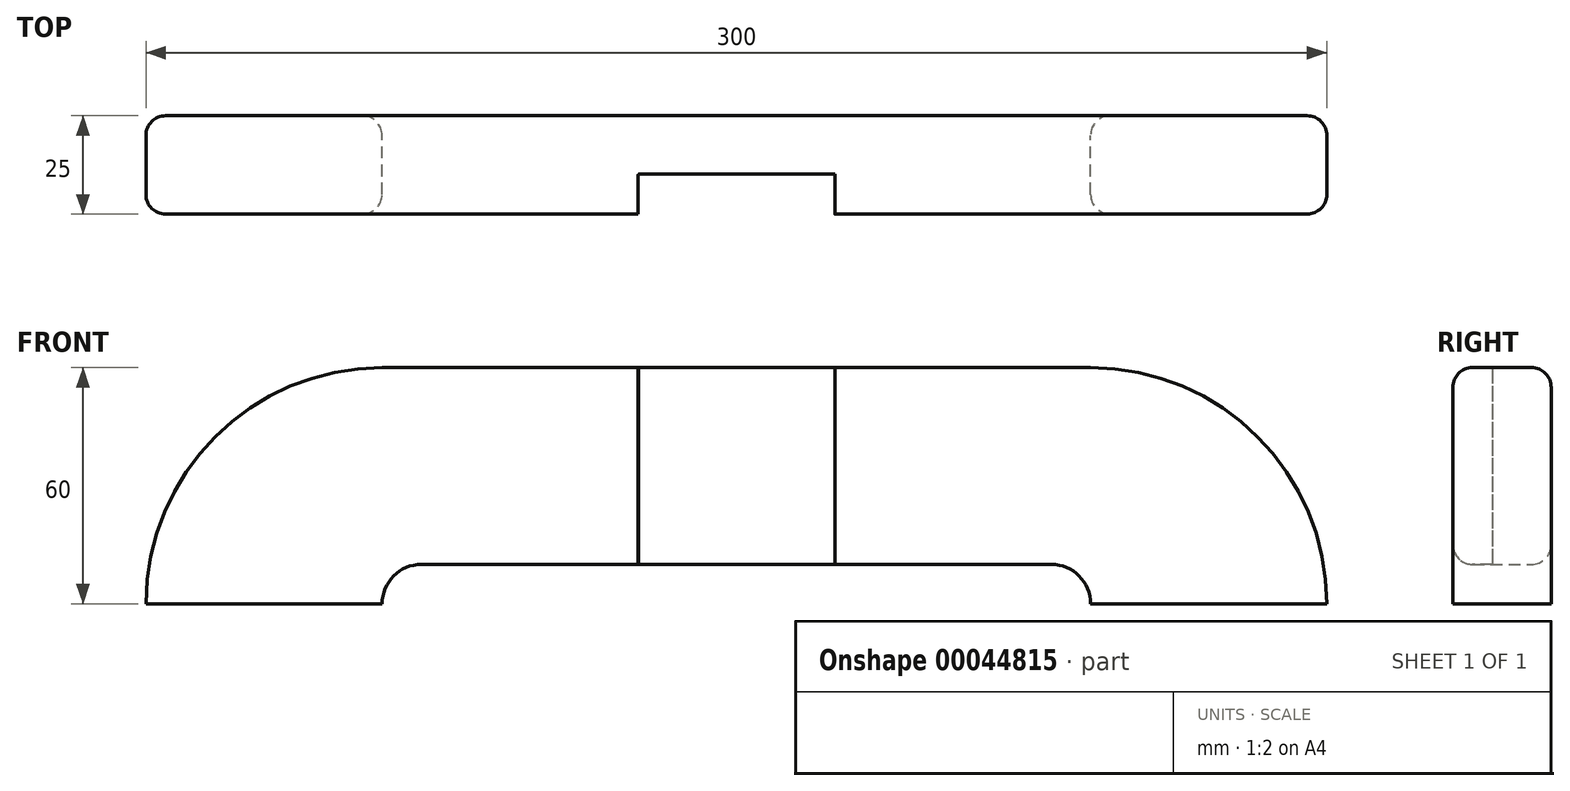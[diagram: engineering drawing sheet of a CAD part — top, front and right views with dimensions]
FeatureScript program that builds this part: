
annotation { "Feature Type Name" : "Feature", "Feature Type Description" : "" }
export const myFeature = defineFeature(function(context is Context, id is Id, definition is map)
    precondition{}
    {
        {
            var Q0;
            Q0=qCreatedBy(makeId("Front.planeOp"),FACE);
            var sketch = newSketch(context, id + "F0", { "sketchPlane" : qUnion([Q0])});
            skLineSegment(sketch, "E0.rect.bottom", {"start": v(90, 25) * mm, "end": v(-90, 25) * mm});
            skLineSegment(sketch, "E0.rect.top", {"start": v(90, -25) * mm, "end": v(-90, -25) * mm});
            skLineSegment(sketch, "E0.rect.left", {"start": v(90, 25) * mm, "end": v(90, -25) * mm});
            skLineSegment(sketch, "E0.rect.right", {"start": v(-90, 25) * mm, "end": v(-90, -25) * mm});
            skPoint(sketch, "E0.rect.middle", {"position": v(0, 0) * mm});
            skLineSegment(sketch, "E1.bottom", {"start": v(-90, 25) * mm, "end": v(-150, 25) * mm});
            skLineSegment(sketch, "E1.top", {"start": v(-90, -35) * mm, "end": v(-150, -35) * mm});
            skLineSegment(sketch, "E1.left", {"start": v(-90, 25) * mm, "end": v(-90, -35) * mm});
            skLineSegment(sketch, "E1.right", {"start": v(-150, 25) * mm, "end": v(-150, -35) * mm});
            skLineSegment(sketch, "E2", {"start": v(0, 42) * mm, "end": v(0, -72.64) * mm});
            skPoint(sketch, "E2.endSnap0", {"position": v(0, -25) * mm});
            skLineSegment(sketch, "E3.MirrorCS", {"start": v(90, 25) * mm, "end": v(90, -35) * mm});
            skLineSegment(sketch, "E4.MirrorCS", {"start": v(90, 25) * mm, "end": v(150, 25) * mm});
            skLineSegment(sketch, "E5.MirrorCS", {"start": v(90, -35) * mm, "end": v(150, -35) * mm});
            skLineSegment(sketch, "E6.MirrorCS", {"start": v(150, 25) * mm, "end": v(150, -35) * mm});
            skSolve(sketch);
        }
        {
            var Q0;
            Q0 = qSketchRegion(id + "F0", true);
            extrude(context, id + "F1", {"entities" : qUnion([Q0]), "depth" : 25 * mm});
        }
        {
            var Q0;
            Q0=makeQuery(id+"F1.opExtrude","SWEPT_EDGE",EDGE,{"disambiguationData":[OSD([sQuery(id+"F0.wireOp",EDGE,"E1.bottom"),sQuery(id+"F0.wireOp",EDGE,"E1.right")])]});
            fillet(context, id + "F2", {"entities" : qUnion([Q0]), "radius" : 60 * mm, "tangentPropagation" : true, "allowEdgeOverflow" : false});
        }
        {
            var Q0;
            Q0=makeQuery(id+"F1.opExtrude","SWEPT_EDGE",EDGE,{"disambiguationData":[OSD([sQuery(id+"F0.wireOp",EDGE,"E0.rect.top"),sQuery(id+"F0.wireOp",EDGE,"E1.left")])]});
            fillet(context, id + "F3", {"entities" : qUnion([Q0]), "radius" : 10 * mm, "tangentPropagation" : true, "allowEdgeOverflow" : false});
        }
        {
            var Q0;
            Q0=makeQuery(id+"F1.opExtrude","SWEPT_EDGE",EDGE,{"disambiguationData":[OSD([sQuery(id+"F0.wireOp",EDGE,"E0.rect.top"),sQuery(id+"F0.wireOp",EDGE,"E3.MirrorCS")])]});
            fillet(context, id + "F4", {"entities" : qUnion([Q0]), "radius" : 10 * mm, "tangentPropagation" : true, "allowEdgeOverflow" : false});
        }
        {
            var Q0;
            Q0=makeQuery(id+"F1.opExtrude","SWEPT_EDGE",EDGE,{"disambiguationData":[OSD([sQuery(id+"F0.wireOp",EDGE,"E4.MirrorCS"),sQuery(id+"F0.wireOp",EDGE,"E6.MirrorCS")])]});
            fillet(context, id + "F5", {"entities" : qUnion([Q0]), "radius" : 60 * mm, "tangentPropagation" : true, "allowEdgeOverflow" : false});
        }
        {
            var Q0;
            {var subQ0=sQuery(id+"F0.wireOp",EDGE,"E4.MirrorCS");var subQ1=sQuery(id+"F0.wireOp",EDGE,"E6.MirrorCS");Q0=makeQuery(id+"F5.opFillet","BLEND_EDGE",EDGE,{"blendedFrom":[makeQuery(id+"F1.opExtrude","SWEPT_EDGE",EDGE,{"disambiguationData":[OSD([subQ0,subQ1])]}),makeQuery(id+"F1.opExtrude","CAP_FACE",FACE,{"disambiguationData":[OSD([sQuery(id+"F0.wireOp",EDGE,"E0.rect.bottom"),sQuery(id+"F0.wireOp",EDGE,"E0.rect.top"),sQuery(id+"F0.wireOp",EDGE,"E1.bottom"),sQuery(id+"F0.wireOp",EDGE,"E1.top"),sQuery(id+"F0.wireOp",EDGE,"E1.left"),sQuery(id+"F0.wireOp",EDGE,"E1.right"),sQuery(id+"F0.wireOp",EDGE,"E3.MirrorCS"),subQ0,sQuery(id+"F0.wireOp",EDGE,"E5.MirrorCS"),subQ1])],"isStart":false})],"blendedInto":[makeQuery(id+"F1.opExtrude","CAP_FACE",FACE,{"disambiguationData":[OSD([sQuery(id+"F0.wireOp",EDGE,"E0.rect.bottom"),sQuery(id+"F0.wireOp",EDGE,"E0.rect.top"),sQuery(id+"F0.wireOp",EDGE,"E1.bottom"),sQuery(id+"F0.wireOp",EDGE,"E1.top"),sQuery(id+"F0.wireOp",EDGE,"E1.left"),sQuery(id+"F0.wireOp",EDGE,"E1.right"),sQuery(id+"F0.wireOp",EDGE,"E3.MirrorCS"),subQ0,sQuery(id+"F0.wireOp",EDGE,"E5.MirrorCS"),subQ1])],"isStart":false})]});}
            fillet(context, id + "F6", {"entities" : qUnion([Q0]), "radius" : 5 * mm, "tangentPropagation" : true, "allowEdgeOverflow" : false});
        }
        {
            var Q0;
            {var subQ0=sQuery(id+"F0.wireOp",EDGE,"E4.MirrorCS");var subQ1=sQuery(id+"F0.wireOp",EDGE,"E6.MirrorCS");Q0=makeQuery(id+"F5.opFillet","BLEND_EDGE",EDGE,{"blendedFrom":[makeQuery(id+"F1.opExtrude","SWEPT_EDGE",EDGE,{"disambiguationData":[OSD([subQ0,subQ1])]}),makeQuery(id+"F1.opExtrude","CAP_FACE",FACE,{"disambiguationData":[OSD([sQuery(id+"F0.wireOp",EDGE,"E0.rect.bottom"),sQuery(id+"F0.wireOp",EDGE,"E0.rect.top"),sQuery(id+"F0.wireOp",EDGE,"E1.bottom"),sQuery(id+"F0.wireOp",EDGE,"E1.top"),sQuery(id+"F0.wireOp",EDGE,"E1.left"),sQuery(id+"F0.wireOp",EDGE,"E1.right"),sQuery(id+"F0.wireOp",EDGE,"E3.MirrorCS"),subQ0,sQuery(id+"F0.wireOp",EDGE,"E5.MirrorCS"),subQ1])],"isStart":true})],"blendedInto":[makeQuery(id+"F1.opExtrude","CAP_FACE",FACE,{"disambiguationData":[OSD([sQuery(id+"F0.wireOp",EDGE,"E0.rect.bottom"),sQuery(id+"F0.wireOp",EDGE,"E0.rect.top"),sQuery(id+"F0.wireOp",EDGE,"E1.bottom"),sQuery(id+"F0.wireOp",EDGE,"E1.top"),sQuery(id+"F0.wireOp",EDGE,"E1.left"),sQuery(id+"F0.wireOp",EDGE,"E1.right"),sQuery(id+"F0.wireOp",EDGE,"E3.MirrorCS"),subQ0,sQuery(id+"F0.wireOp",EDGE,"E5.MirrorCS"),subQ1])],"isStart":true})]});}
            fillet(context, id + "F7", {"entities" : qUnion([Q0]), "radius" : 5 * mm, "tangentPropagation" : true, "allowEdgeOverflow" : false});
        }
        {
            var Q0;
            {var subQ0=sQuery(id+"F0.wireOp",EDGE,"E0.rect.top");var subQ1=sQuery(id+"F0.wireOp",EDGE,"E3.MirrorCS");Q0=makeQuery(id+"F4.opFillet","BLEND_EDGE",EDGE,{"blendedFrom":[makeQuery(id+"F1.opExtrude","SWEPT_EDGE",EDGE,{"disambiguationData":[OSD([subQ0,subQ1])]}),makeQuery(id+"F1.opExtrude","CAP_FACE",FACE,{"disambiguationData":[OSD([sQuery(id+"F0.wireOp",EDGE,"E0.rect.bottom"),subQ0,sQuery(id+"F0.wireOp",EDGE,"E1.bottom"),sQuery(id+"F0.wireOp",EDGE,"E1.top"),sQuery(id+"F0.wireOp",EDGE,"E1.left"),sQuery(id+"F0.wireOp",EDGE,"E1.right"),subQ1,sQuery(id+"F0.wireOp",EDGE,"E4.MirrorCS"),sQuery(id+"F0.wireOp",EDGE,"E5.MirrorCS"),sQuery(id+"F0.wireOp",EDGE,"E6.MirrorCS")])],"isStart":true})],"blendedInto":[makeQuery(id+"F1.opExtrude","CAP_FACE",FACE,{"disambiguationData":[OSD([sQuery(id+"F0.wireOp",EDGE,"E0.rect.bottom"),subQ0,sQuery(id+"F0.wireOp",EDGE,"E1.bottom"),sQuery(id+"F0.wireOp",EDGE,"E1.top"),sQuery(id+"F0.wireOp",EDGE,"E1.left"),sQuery(id+"F0.wireOp",EDGE,"E1.right"),subQ1,sQuery(id+"F0.wireOp",EDGE,"E4.MirrorCS"),sQuery(id+"F0.wireOp",EDGE,"E5.MirrorCS"),sQuery(id+"F0.wireOp",EDGE,"E6.MirrorCS")])],"isStart":true})]});}
            var Q1;
            Q1=makeQuery(id+"F1.opExtrude","CAP_EDGE",EDGE,{"disambiguationData":[OSD([sQuery(id+"F0.wireOp",EDGE,"E0.rect.top")])],"isStart":false});
            fillet(context, id + "F8", {"entities" : qUnion([Q0, Q1]), "radius" : 5 * mm, "tangentPropagation" : true, "allowEdgeOverflow" : false});
        }
        {
            var Q0;
            Q0=makeQuery(id+"F1.opExtrude","CAP_FACE",FACE,{"disambiguationData":[OSD([sQuery(id+"F0.wireOp",EDGE,"E0.rect.bottom"),sQuery(id+"F0.wireOp",EDGE,"E0.rect.top"),sQuery(id+"F0.wireOp",EDGE,"E1.bottom"),sQuery(id+"F0.wireOp",EDGE,"E1.top"),sQuery(id+"F0.wireOp",EDGE,"E1.left"),sQuery(id+"F0.wireOp",EDGE,"E1.right"),sQuery(id+"F0.wireOp",EDGE,"E3.MirrorCS"),sQuery(id+"F0.wireOp",EDGE,"E4.MirrorCS"),sQuery(id+"F0.wireOp",EDGE,"E5.MirrorCS"),sQuery(id+"F0.wireOp",EDGE,"E6.MirrorCS")])],"isStart":false});
            var sketch = newSketch(context, id + "F9", { "sketchPlane" : qUnion([Q0])});
            skLineSegment(sketch, "E7.rect.bottom", {"start": v(25, -25) * mm, "end": v(-25, -25) * mm});
            skLineSegment(sketch, "E7.rect.top", {"start": v(25, 25) * mm, "end": v(-25, 25) * mm});
            skLineSegment(sketch, "E7.rect.left", {"start": v(25, -25) * mm, "end": v(25, 25) * mm});
            skLineSegment(sketch, "E7.rect.right", {"start": v(-25, -25) * mm, "end": v(-25, 25) * mm});
            skPoint(sketch, "E7.rect.middle", {"position": v(0, 0) * mm});
            skSolve(sketch);
        }
        {
            var Q0;
            {var subQ6=sQuery(id+"F9.wireOp",EDGE,"E7.rect.bottom");Q0=makeQuery(id+"F9.imprint","IMPRINT",FACE,{"disambiguationData":[TD([[makeQuery(id+"F9.imprint","IMPRINT",EDGE,{"derivedFrom":subQ6}),-1.0]])]});}
            var Q1;
            {var subQ6=sQuery(id+"F9.wireOp",EDGE,"E7.rect.top");Q1=makeQuery(id+"F9.imprint","IMPRINT",FACE,{"disambiguationData":[TD([[makeQuery(id+"F9.imprint","IMPRINT",EDGE,{"derivedFrom":subQ6}),1.0]])]});}
            var Q2;
            {var subQ0=sQuery(id+"F0.wireOp",EDGE,"E0.rect.bottom");var subQ1=sQuery(id+"F0.wireOp",EDGE,"E1.bottom");var subQ2=sQuery(id+"F0.wireOp",EDGE,"E4.MirrorCS");var subQ3=sQuery(id+"F0.wireOp",EDGE,"E0.rect.top");var subQ4=makeQuery(id+"F1.opExtrude","CAP_FACE",FACE,{"disambiguationData":[OSD([subQ0,subQ3,subQ1,sQuery(id+"F0.wireOp",EDGE,"E1.top"),sQuery(id+"F0.wireOp",EDGE,"E1.left"),sQuery(id+"F0.wireOp",EDGE,"E1.right"),sQuery(id+"F0.wireOp",EDGE,"E3.MirrorCS"),subQ2,sQuery(id+"F0.wireOp",EDGE,"E5.MirrorCS"),sQuery(id+"F0.wireOp",EDGE,"E6.MirrorCS")])],"isStart":false});var subQ8=sQuery(id+"F9.wireOp",EDGE,"E7.rect.left");var subQ10=makeQuery(id+"F8.opFillet","BLEND_EDGE",EDGE,{"blendedFrom":[makeQuery(id+"F1.opExtrude","CAP_EDGE",EDGE,{"disambiguationData":[OSD([subQ3])],"isStart":false}),subQ4],"blendedInto":[subQ4]});var subQ12=makeQuery(id+"F9.imprint","INTERSECT",VERTEX,{"derivedFrom":[subQ10,subQ8]});Q2=makeQuery(id+"F9.imprint","IMPRINT",FACE,{"disambiguationData":[TD([[makeQuery(id+"F9.imprint","IMPRINT",EDGE,{"disambiguationData":[TD([[subQ12,-1.0]])],"derivedFrom":subQ8}),1.0]])]});}
            extrude(context, id + "F10", {"entities" : qUnion([Q0, Q1, Q2]), "operationType" : NewBodyOperationType.ADD, "oppositeDirection" : true, "depth" : 10 * mm});
        }
        {
            var Q0;
            Q0=makeQuery(id+"F10.boolean.opBoolean","MERGE",FACE,{"derivedFrom":[makeQuery(id+"F1.opExtrude","SWEPT_FACE",FACE,{"disambiguationData":[OSD([sQuery(id+"F0.wireOp",EDGE,"E0.rect.bottom"),sQuery(id+"F0.wireOp",EDGE,"E1.bottom"),sQuery(id+"F0.wireOp",EDGE,"E4.MirrorCS")])]}),makeQuery(id+"F10.opExtrude","SWEPT_FACE",FACE,{"disambiguationData":[OSD([sQuery(id+"F9.wireOp",EDGE,"E7.rect.top")])]})]});
            var sketch = newSketch(context, id + "F11", { "sketchPlane" : qUnion([Q0])});
            skLineSegment(sketch, "E8", {"start": v(-25, -20) * mm, "end": v(-25, -5) * mm});
            skSolve(sketch);
        }
        {
            var Q0;
            Q0=makeQuery(id+"F10.boolean.opBoolean","MERGE",FACE,{"derivedFrom":[makeQuery(id+"F1.opExtrude","SWEPT_FACE",FACE,{"disambiguationData":[OSD([sQuery(id+"F0.wireOp",EDGE,"E0.rect.top")])]}),makeQuery(id+"F10.opExtrude","SWEPT_FACE",FACE,{"disambiguationData":[OSD([sQuery(id+"F9.wireOp",EDGE,"E7.rect.bottom")])]})]});
            var sketch = newSketch(context, id + "F12", { "sketchPlane" : qUnion([Q0])});
            skLineSegment(sketch, "E9", {"start": v(-25, 20) * mm, "end": v(-25, 5) * mm});
            skSolve(sketch);
        }
        {
            var Q0;
            {var subQ7=sQuery(id+"F11.wireOp",EDGE,"E8");Q0=makeQuery(id+"F11.imprint","IMPRINT",FACE,{"disambiguationData":[TD([[makeQuery(id+"F11.imprint","IMPRINT",EDGE,{"derivedFrom":subQ7}),-1.0]])]});}
            var sketch = newSketch(context, id + "F13", { "sketchPlane" : qUnion([Q0])});
            skLineSegment(sketch, "E10.bottom", {"start": v(-24.9, -24.82) * mm, "end": v(25.1, -24.82) * mm});
            skLineSegment(sketch, "E10.top", {"start": v(-24.9, -14.82) * mm, "end": v(25.1, -14.82) * mm});
            skLineSegment(sketch, "E10.left", {"start": v(-24.9, -24.82) * mm, "end": v(-24.9, -14.82) * mm});
            skLineSegment(sketch, "E10.right", {"start": v(25.1, -24.82) * mm, "end": v(25.1, -14.82) * mm});
            skSolve(sketch);
        }
        {
            var Q0;
            Q0 = qSketchRegion(id + "F13", true);
            extrude(context, id + "F14", {"entities" : qUnion([Q0]), "operationType" : NewBodyOperationType.REMOVE, "endBound" : BoundingType.THROUGH_ALL, "oppositeDirection" : true, "depth" : 25 * mm});
        }
        {
            var Q0;
            Q0=makeQuery(id+"F10.boolean.opBoolean","MERGE",FACE,{"derivedFrom":[makeQuery(id+"F1.opExtrude","CAP_FACE",FACE,{"disambiguationData":[OSD([sQuery(id+"F0.wireOp",EDGE,"E0.rect.bottom"),sQuery(id+"F0.wireOp",EDGE,"E0.rect.top"),sQuery(id+"F0.wireOp",EDGE,"E1.bottom"),sQuery(id+"F0.wireOp",EDGE,"E1.top"),sQuery(id+"F0.wireOp",EDGE,"E1.left"),sQuery(id+"F0.wireOp",EDGE,"E1.right"),sQuery(id+"F0.wireOp",EDGE,"E3.MirrorCS"),sQuery(id+"F0.wireOp",EDGE,"E4.MirrorCS"),sQuery(id+"F0.wireOp",EDGE,"E5.MirrorCS"),sQuery(id+"F0.wireOp",EDGE,"E6.MirrorCS")])],"isStart":false}),makeQuery(id+"F10.opExtrude","CAP_FACE",FACE,{"disambiguationData":[OSD([sQuery(id+"F9.wireOp",EDGE,"E7.rect.bottom"),sQuery(id+"F9.wireOp",EDGE,"E7.rect.top"),sQuery(id+"F9.wireOp",EDGE,"E7.rect.left"),sQuery(id+"F9.wireOp",EDGE,"E7.rect.right")])],"isStart":true})]});
            var sketch = newSketch(context, id + "F15", { "sketchPlane" : qUnion([Q0])});
            skLineSegment(sketch, "E11", {"start": v(-25, 25) * mm, "end": v(-25, -25) * mm});
            skLineSegment(sketch, "E12", {"start": v(-25, -25) * mm, "end": v(25, -25) * mm});
            skLineSegment(sketch, "E13", {"start": v(25, -25) * mm, "end": v(25, 25) * mm});
            skLineSegment(sketch, "E14", {"start": v(25, 25) * mm, "end": v(-25, 25) * mm});
            skSolve(sketch);
        }
        {
            var Q0;
            {var subQ28=sQuery(id+"F15.wireOp",EDGE,"E12");Q0=makeQuery(id+"F15.imprint","IMPRINT",FACE,{"disambiguationData":[TD([[makeQuery(id+"F15.imprint","IMPRINT",EDGE,{"derivedFrom":subQ28}),-1.0]])]});}
            extrude(context, id + "F16", {"entities" : qUnion([Q0]), "operationType" : NewBodyOperationType.REMOVE, "oppositeDirection" : true, "depth" : 10 * mm});
        }
    });
